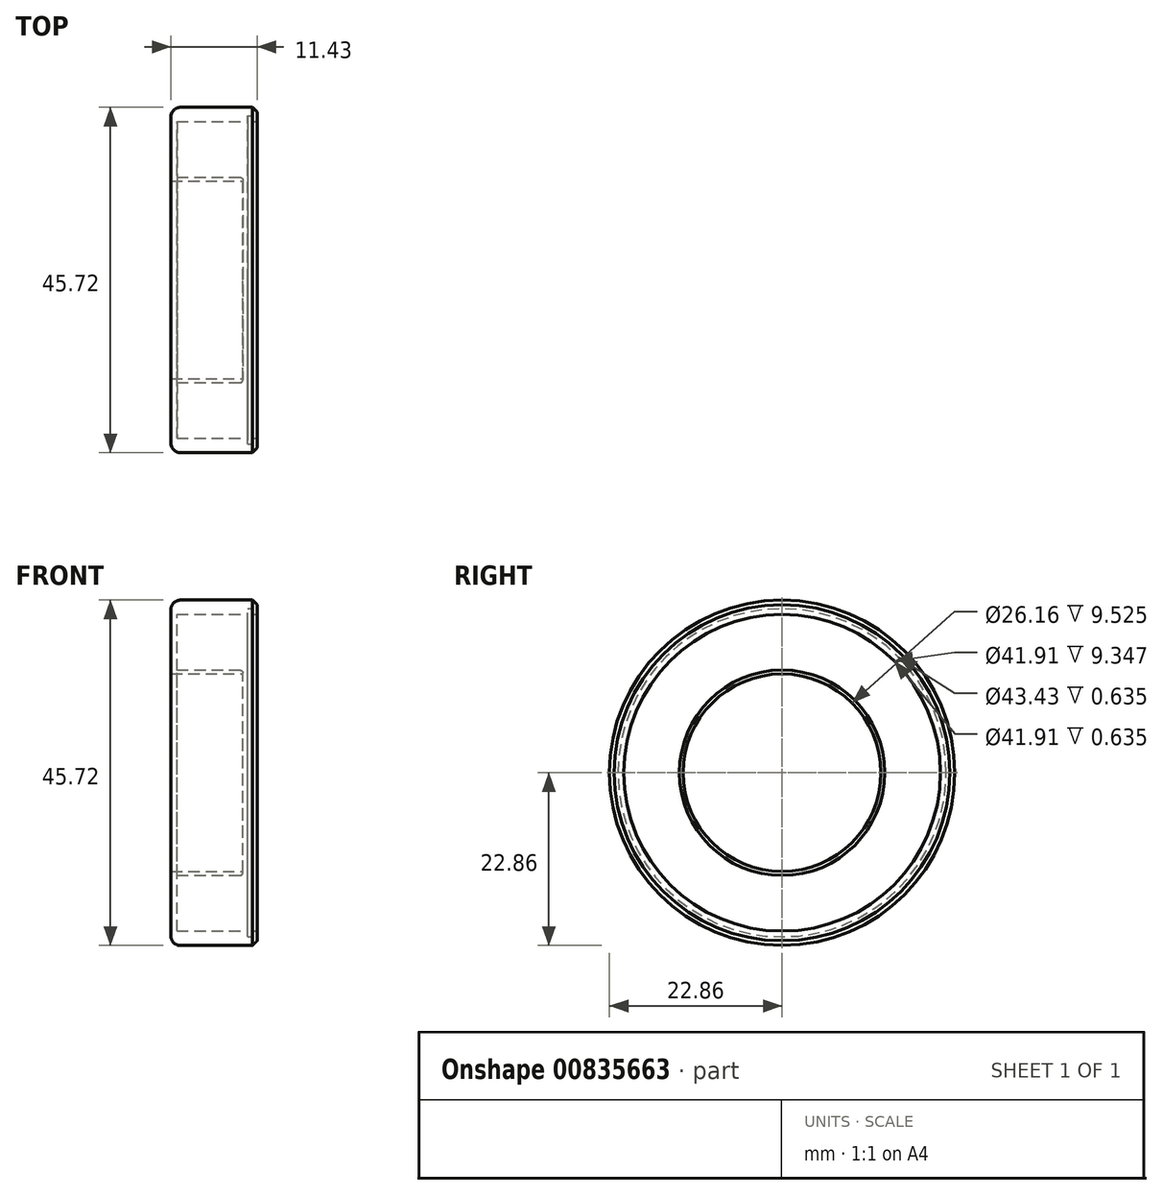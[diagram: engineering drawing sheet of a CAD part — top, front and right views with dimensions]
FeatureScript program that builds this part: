
annotation { "Feature Type Name" : "Feature", "Feature Type Description" : "" }
export const myFeature = defineFeature(function(context is Context, id is Id, definition is map)
    precondition{}
    {
        {
            var Q0;
            Q0=qCreatedBy(makeId("Front.planeOp"),FACE);
            var sketch = newSketch(context, id + "F0", { "sketchPlane" : qUnion([Q0])});
            skLineSegment(sketch, "E0", {"start": v(11.43, 22.86) * mm, "end": v(0, 22.86) * mm});
            skLineSegment(sketch, "E1", {"start": v(0, 22.86) * mm, "end": v(0, 13.08) * mm});
            skLineSegment(sketch, "E2", {"start": v(0, 13.08) * mm, "end": v(9.53, 13.08) * mm});
            skLineSegment(sketch, "E3", {"start": v(9.52, 13.08) * mm, "end": v(9.52, 13.59) * mm});
            skLineSegment(sketch, "E4", {"start": v(9.53, 13.59) * mm, "end": v(0.81, 13.59) * mm});
            skLineSegment(sketch, "E5", {"start": v(0.81, 13.59) * mm, "end": v(0.81, 20.96) * mm});
            skLineSegment(sketch, "E6", {"start": v(0.81, 20.96) * mm, "end": v(10.16, 20.96) * mm});
            skLineSegment(sketch, "E7", {"start": v(10.16, 20.96) * mm, "end": v(10.16, 21.72) * mm});
            skLineSegment(sketch, "E8", {"start": v(10.16, 21.72) * mm, "end": v(10.8, 21.72) * mm});
            skLineSegment(sketch, "E9", {"start": v(10.8, 21.72) * mm, "end": v(10.8, 20.95) * mm});
            skLineSegment(sketch, "E10", {"start": v(10.8, 20.95) * mm, "end": v(11.43, 20.95) * mm});
            skLineSegment(sketch, "E11", {"start": v(11.43, 20.95) * mm, "end": v(11.43, 22.86) * mm});
            skLineSegment(sketch, "E12", {"start": v(0, 0) * mm, "end": v(18.03, 0) * mm, "construction": true});
            skSolve(sketch);
        }
        {
            var Q0;
            Q0 = qConstructionFilter(qBodyType(qCreatedBy(id + "F0" ,EDGE), BodyType.WIRE), ConstructionObject.NO);
            var Q1;
            Q1=sQuery(id+"F0.wireOp",EDGE,"E12");
            revolve(context, id + "F1", {"bodyType" : ToolBodyType.SURFACE, "surfaceOperationType" : NewSurfaceOperationType.NEW, "surfaceEntities" : qUnion([Q0]), "axis" : qUnion([Q1]), "revolveType" : RevolveType.FULL});
        }
        {
            var Q0;
            Q0=makeQuery(id+"F1.opRevolve","SWEPT_EDGE",EDGE,{"disambiguationData":[OSD([sQuery(id+"F0.wireOp",VERTEX,"E4.start")])]});
            fillet(context, id + "F2", {"entities" : qUnion([Q0]), "radius" : 0.38 * mm, "tangentPropagation" : true, "allowEdgeOverflow" : false});
        }
        {
            var Q0;
            Q0=makeQuery(id+"F1.opRevolve","SWEPT_EDGE",EDGE,{"disambiguationData":[OSD([sQuery(id+"F0.wireOp",VERTEX,"E11.end")])]});
            chamfer(context, id + "F3", {"entities" : qUnion([Q0]), "width" : 0.64 * mm, "tangentPropagation" : true});
        }
        {
            var Q0;
            Q0=makeQuery(id+"F1.opRevolve","SWEPT_EDGE",EDGE,{"disambiguationData":[OSD([sQuery(id+"F0.wireOp",VERTEX,"E1.start")])]});
            fillet(context, id + "F4", {"entities" : qUnion([Q0]), "radius" : 1.27 * mm, "tangentPropagation" : true, "allowEdgeOverflow" : false});
        }
    });
